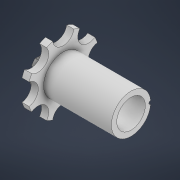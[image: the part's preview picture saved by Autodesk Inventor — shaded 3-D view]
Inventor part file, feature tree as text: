
AUTODESK INVENTOR PART (.ipt)
format: ipt  version: 2021 (Build 250183000, 183)  size: 290,816 bytes
history: native  units: in
note: dims shown in document units (in); Inventor stores cm internally (conversion verified against a paired STEP export)
features: extrude x7, sketch x7, plane x3, pattern_circular x2
ambient origin geometry x8: Origin, YZ Plane, XZ Plane, XY Plane, X Axis, Y Axis, Z Axis, Center Point
bodies: Solid1 (feature_tree)
feature tree (19):
  extrude  "Extrusion1"  Depth=0.8465in TaperAngle=0.0deg
  extrude  "Extrusion2"  Depth=0.4724in TaperAngle=0.0deg
  extrude  "Extrusion3"  Depth=0.4724in TaperAngle=0.0deg
  extrude  "Extrusion4"  TaperAngle=0.0deg  [1 undecoded]
  plane  "Work Plane1"
  extrude  "Extrusion5"  Depth=0.4331in
  plane  "Work Plane3"
  extrude  "Extrusion7"  [1 undecoded]
  pattern_circular  "Circular Pattern1"  Count=2  [1 undecoded]
  plane  "Work Plane4"
  extrude  "Extrusion8"  Depth=0.0591in
  pattern_circular  "Circular Pattern2"  [2 undecoded]
  sketch  "Sketch1"  dims[d1=0.4331in d2=0.8465in d3=0.0in]
  sketch  "Sketch2"  dims[d4=0.315in d5=0.4724in d6=0.0in]
  sketch  "Sketch3"  dims[d7=0.1969in d8=0.4724in d9=0.0in]
  sketch  "Sketch4"  dims[d10=0.0394in d11=0.0in]
  sketch  "Sketch5"  dims[d12=0.2165in d13=0.4331in]
  sketch  "Sketch8"  dims[d14=0.5906in d15=0.0in d16=-0.0197in d17=0.7874in]
  sketch  "Sketch9"  dims[d18=0.2784in d19=0.2784in d20=0.2362in d22=3.1496in d24=360.0deg d26=0.7874in d27=0.3937in d28=3.1496in d30=360.0deg d32=0.0787in d33=0.0in d44=0.0in d45=0.0944in d46=0.0984in d47=0.0984in d48=0.0547in d49=0.0547in d50=0.0591in d51=0.0in d52=3.1496in d53=360.0deg d67=0.0591in d68=0.0in d69=0.0502in d70=3.1496in d71=360.0deg]
note: 5 required parameter values undecoded (feature->parameter linkage not recoverable at this tier; creation-order binding heuristic only, values carry confidence <= 0.55)
